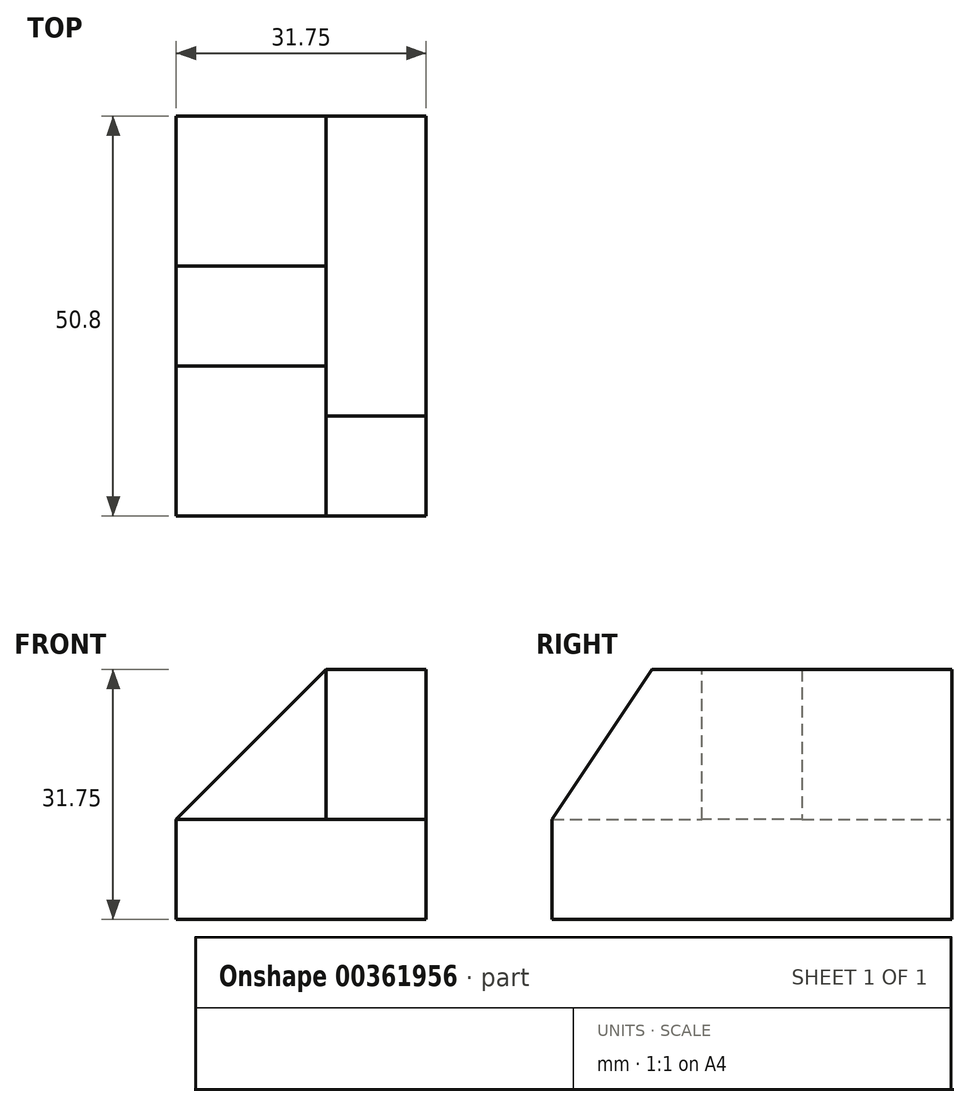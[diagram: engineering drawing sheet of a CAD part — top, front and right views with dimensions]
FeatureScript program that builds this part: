
annotation { "Feature Type Name" : "Feature", "Feature Type Description" : "" }
export const myFeature = defineFeature(function(context is Context, id is Id, definition is map)
    precondition{}
    {
        {
            var Q0;
            Q0=qCreatedBy(makeId("Front.planeOp"),FACE);
            var sketch = newSketch(context, id + "F0", { "sketchPlane" : qUnion([Q0])});
            skLineSegment(sketch, "E0", {"start": v(0, 0) * mm, "end": v(0, 12.7) * mm});
            skLineSegment(sketch, "E1", {"start": v(0, 12.7) * mm, "end": v(19.05, 12.7) * mm});
            skLineSegment(sketch, "E2", {"start": v(19.05, 12.7) * mm, "end": v(19.05, 31.75) * mm});
            skLineSegment(sketch, "E3", {"start": v(19.05, 31.75) * mm, "end": v(31.75, 31.75) * mm});
            skLineSegment(sketch, "E4", {"start": v(31.75, 31.75) * mm, "end": v(31.75, 0) * mm});
            skLineSegment(sketch, "E5", {"start": v(31.75, 0) * mm, "end": v(0, 0) * mm});
            skSolve(sketch);
        }
        {
            var Q0;
            Q0=makeQuery(id+"F0.imprint","IMPRINT",FACE,{"disambiguationData":[TD([[makeQuery(id+"F0.imprint","IMPRINT",EDGE,{"derivedFrom":sQuery(id+"F0.wireOp",EDGE,"E0")}),-1.0]])]});
            extrude(context, id + "F1", {"entities" : qUnion([Q0]), "depth" : 50.8 * mm});
        }
        {
            var Q0;
            Q0=makeQuery(id+"F1.opExtrude","SWEPT_FACE",FACE,{"disambiguationData":[OSD([sQuery(id+"F0.wireOp",EDGE,"E2")])]});
            var sketch = newSketch(context, id + "F2", { "sketchPlane" : qUnion([Q0])});
            skLineSegment(sketch, "E6", {"start": v(38.1, 31.75) * mm, "end": v(50.8, 12.7) * mm});
            skSolve(sketch);
        }
        {
            var Q0;
            {var subQ0=sQuery(id+"F2.wireOp",EDGE,"E6");Q0=makeQuery(id+"F2.imprint","IMPRINT",FACE,{"disambiguationData":[TD([[makeQuery(id+"F2.imprint","IMPRINT",EDGE,{"derivedFrom":subQ0}),1.0]])]});}
            extrude(context, id + "F3", {"entities" : qUnion([Q0]), "operationType" : NewBodyOperationType.REMOVE, "oppositeDirection" : true, "depth" : 25.4 * mm});
        }
        {
            var Q0;
            Q0=makeQuery(id+"F1.opExtrude","SWEPT_FACE",FACE,{"disambiguationData":[OSD([sQuery(id+"F0.wireOp",EDGE,"E2")])]});
            var sketch = newSketch(context, id + "F4", { "sketchPlane" : qUnion([Q0])});
            skLineSegment(sketch, "E7", {"start": v(19.05, 31.75) * mm, "end": v(19.05, 12.7) * mm});
            skLineSegment(sketch, "E8", {"start": v(19.05, 12.7) * mm, "end": v(31.75, 12.7) * mm});
            skLineSegment(sketch, "E9", {"start": v(31.75, 12.7) * mm, "end": v(31.75, 31.75) * mm});
            skLineSegment(sketch, "E10", {"start": v(31.75, 31.75) * mm, "end": v(19.05, 31.75) * mm});
            skSolve(sketch);
        }
        {
            var Q0;
            Q0 = qSketchRegion(id + "F4", true);
            extrude(context, id + "F5", {"entities" : qUnion([Q0]), "operationType" : NewBodyOperationType.ADD, "depth" : 19.05 * mm});
        }
        {
            var Q0;
            Q0=makeQuery(id+"F5.opExtrude","SWEPT_FACE",FACE,{"disambiguationData":[OSD([sQuery(id+"F4.wireOp",EDGE,"E9")])]});
            var sketch = newSketch(context, id + "F6", { "sketchPlane" : qUnion([Q0])});
            skLineSegment(sketch, "E11", {"start": v(0, 12.7) * mm, "end": v(19.05, 31.75) * mm});
            skSolve(sketch);
        }
        {
            var Q0;
            Q0=makeQuery(id+"F6.imprint","IMPRINT",FACE,{"disambiguationData":[TD([[makeQuery(id+"F6.imprint","IMPRINT",EDGE,{"derivedFrom":sQuery(id+"F6.wireOp",EDGE,"E11")}),1.0]])]});
            extrude(context, id + "F7", {"entities" : qUnion([Q0]), "operationType" : NewBodyOperationType.REMOVE, "oppositeDirection" : true, "depth" : 25.4 * mm});
        }
    });
